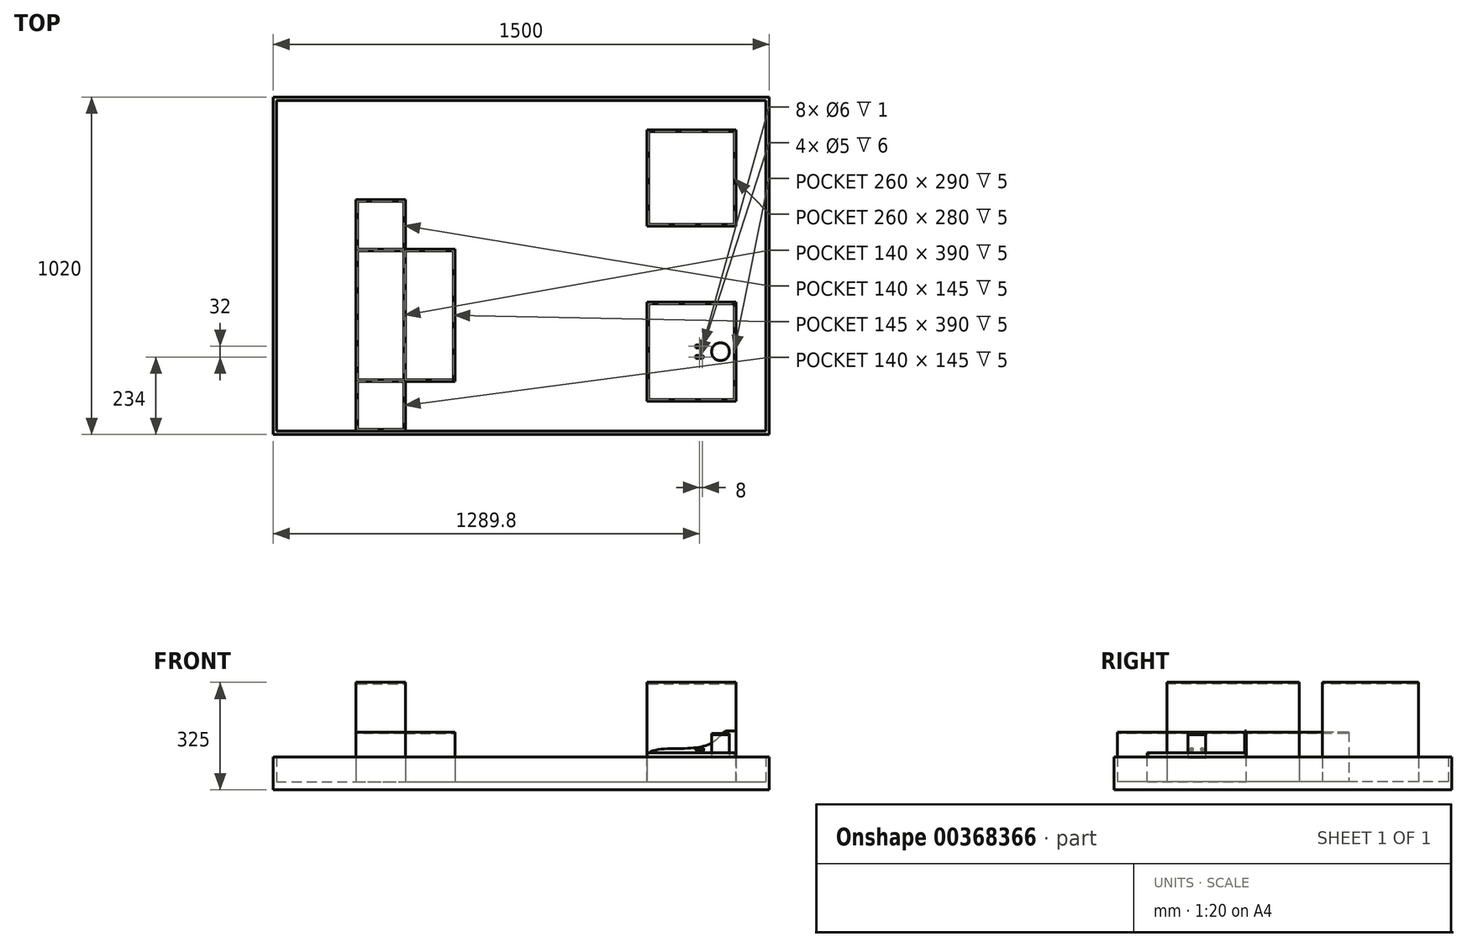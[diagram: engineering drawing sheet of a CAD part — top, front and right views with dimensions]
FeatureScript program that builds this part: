
annotation { "Feature Type Name" : "Feature", "Feature Type Description" : "" }
export const myFeature = defineFeature(function(context is Context, id is Id, definition is map)
    precondition{}
    {
        {
            var Q0;
            Q0=qCreatedBy(makeId("Top.planeOp"),FACE);
            var sketch = newSketch(context, id + "F0", { "sketchPlane" : qUnion([Q0])});
            skCircle(sketch, "E0", {"center": v(0, 0) * mm, "radius": 27.2 * mm});
            skSolve(sketch);
        }
        {
            var Q0;
            Q0=qSketchRegion(id+"F0",true);
            extrude(context, id + "F1", {"entities" : qUnion([Q0]), "depth" : 2.83 * mm});
        }
        {
            var Q0;
            Q0=makeQuery(id+"F1.opExtrude","CAP_FACE",FACE,{"disambiguationData":[OSD([sQuery(id+"F0.wireOp",EDGE,"E0")])],"isStart":false});
            var sketch = newSketch(context, id + "F2", { "sketchPlane" : qUnion([Q0])});
            skCircle(sketch, "E1", {"center": v(0, 0) * mm, "radius": 26.4 * mm});
            skSolve(sketch);
        }
        {
            var Q0;
            Q0=qSketchRegion(id+"F2",true);
            extrude(context, id + "F3", {"entities" : qUnion([Q0]), "operationType" : NewBodyOperationType.ADD, "depth" : 67.36 * mm});
        }
        {
            var Q0;
            Q0=makeQuery(id+"F3.opExtrude","CAP_FACE",FACE,{"disambiguationData":[OSD([sQuery(id+"F2.wireOp",EDGE,"E1")])],"isStart":false});
            var sketch = newSketch(context, id + "F4", { "sketchPlane" : qUnion([Q0])});
            skCircle(sketch, "E2", {"center": v(0, 0) * mm, "radius": 27.2 * mm});
            skSolve(sketch);
        }
        {
            var Q0;
            Q0=qSketchRegion(id+"F4",true);
            extrude(context, id + "F5", {"entities" : qUnion([Q0]), "operationType" : NewBodyOperationType.ADD, "depth" : 2.83 * mm});
        }
        {
            var Q0;
            Q0=makeQuery(id+"F5.opExtrude","CAP_FACE",FACE,{"disambiguationData":[OSD([sQuery(id+"F4.wireOp",EDGE,"E2")])],"isStart":false});
            var sketch = newSketch(context, id + "F6", { "sketchPlane" : qUnion([Q0])});
            skSolve(sketch);
        }
        {
            var Q0;
            Q0=qCreatedBy(makeId("Top.planeOp"),FACE);
            cPlane(context, id + "F7", {"entities" : qUnion([Q0]), "cplaneType" : CPlaneType.OFFSET, "offset" : 25 * mm, "width" : 150 * mm, "height" : 150 * mm});
        }
        {
            var Q0;
            Q0=qCreatedBy(makeId("Top.planeOp"),FACE);
            var sketch = newSketch(context, id + "F8", { "sketchPlane" : qUnion([Q0])});
            skLineSegment(sketch, "E3.bottom", {"start": v(-222.8, -150) * mm, "end": v(47.2, -150) * mm});
            skLineSegment(sketch, "E3.top", {"start": v(-222.8, 150) * mm, "end": v(47.2, 150) * mm});
            skLineSegment(sketch, "E3.left", {"start": v(-222.8, -150) * mm, "end": v(-222.8, 150) * mm});
            skLineSegment(sketch, "E3.right", {"start": v(47.2, -150) * mm, "end": v(47.2, 150) * mm});
            skSolve(sketch);
        }
        {
            var Q0;
            Q0=qSketchRegion(id+"F8",true);
            extrude(context, id + "F9", {"entities" : qUnion([Q0]), "oppositeDirection" : true, "depth" : 72 * mm});
        }
        {
            var Q0;
            Q0=makeQuery(id+"F9.opExtrude","CAP_FACE",FACE,{"disambiguationData":[OSD([sQuery(id+"F8.wireOp",EDGE,"E3.bottom"),sQuery(id+"F8.wireOp",EDGE,"E3.top"),sQuery(id+"F8.wireOp",EDGE,"E3.left"),sQuery(id+"F8.wireOp",EDGE,"E3.right")])],"isStart":true});
            var sketch = newSketch(context, id + "F10", { "sketchPlane" : qUnion([Q0])});
            skLineSegment(sketch, "E4.bottom", {"start": v(-222.8, -150) * mm, "end": v(47.2, -150) * mm});
            skLineSegment(sketch, "E4.top", {"start": v(-222.8, -145) * mm, "end": v(42.2, -145) * mm});
            skLineSegment(sketch, "E4.left", {"start": v(-222.8, -150) * mm, "end": v(-222.8, -145) * mm});
            skLineSegment(sketch, "E5.bottom", {"start": v(47.2, 150) * mm, "end": v(42.2, 150) * mm});
            skLineSegment(sketch, "E5.left", {"start": v(47.2, 150) * mm, "end": v(47.2, -150) * mm});
            skLineSegment(sketch, "E5.right", {"start": v(42.2, 150) * mm, "end": v(42.2, -145) * mm});
            skSolve(sketch);
        }
        {
            var Q0;
            Q0=qSketchRegion(id+"F10",true);
            extrude(context, id + "F11", {"entities" : qUnion([Q0]), "operationType" : NewBodyOperationType.ADD, "depth" : 15 * mm});
        }
        {
            var Q0;
            Q0=makeQuery(id+"F11.boolean.opBoolean","MERGE",FACE,{"derivedFrom":[makeQuery(id+"F9.opExtrude","SWEPT_FACE",FACE,{"disambiguationData":[OSD([sQuery(id+"F8.wireOp",EDGE,"E3.top")])]}),makeQuery(id+"F11.opExtrude","SWEPT_FACE",FACE,{"disambiguationData":[OSD([sQuery(id+"F10.wireOp",EDGE,"E5.bottom")])]})]});
            var sketch = newSketch(context, id + "F12", { "sketchPlane" : qUnion([Q0])});
            skLineSegment(sketch, "E6", {"start": v(-47.2, 81.36) * mm, "end": v(-21.31, 81.36) * mm});
            skFitSpline(sketch, "E7", {"points": [v(-21.31, 81.36) * mm, v(15.24, 52.01) * mm, v(114.14, 28.17) * mm, v(222.8, 0) * mm], "startDerivative": vector(181.02, 0.3) * mm, "endDerivative": vector(-1.73, -239.85) * mm});
            skLineSegment(sketch, "E8", {"start": v(-47.2, 81.36) * mm, "end": v(-47.2, -72) * mm});
            skLineSegment(sketch, "E9", {"start": v(-47.2, -72) * mm, "end": v(222.8, -72) * mm});
            skLineSegment(sketch, "E10", {"start": v(222.8, -72) * mm, "end": v(222.8, 0) * mm});
            skSolve(sketch);
        }
        {
            var Q0;
            Q0=qSketchRegion(id+"F12",true);
            extrude(context, id + "F13", {"entities" : qUnion([Q0]), "operationType" : NewBodyOperationType.ADD, "oppositeDirection" : true, "depth" : 5 * mm});
        }
        {
            var Q0;
            Q0=makeQuery(id+"F9.opExtrude","CAP_FACE",FACE,{"disambiguationData":[OSD([sQuery(id+"F8.wireOp",EDGE,"E3.bottom"),sQuery(id+"F8.wireOp",EDGE,"E3.top"),sQuery(id+"F8.wireOp",EDGE,"E3.left"),sQuery(id+"F8.wireOp",EDGE,"E3.right")])],"isStart":true});
            var sketch = newSketch(context, id + "F14", { "sketchPlane" : qUnion([Q0])});
            skLineSegment(sketch, "E11.bottom", {"start": v(-222.8, 145) * mm, "end": v(-217.8, 145) * mm});
            skLineSegment(sketch, "E11.top", {"start": v(-222.8, -145) * mm, "end": v(-217.8, -145) * mm});
            skLineSegment(sketch, "E11.left", {"start": v(-222.8, 145) * mm, "end": v(-222.8, -145) * mm});
            skLineSegment(sketch, "E11.right", {"start": v(-217.8, 145) * mm, "end": v(-217.8, -145) * mm});
            skSolve(sketch);
        }
        {
            var Q0;
            Q0=qSketchRegion(id+"F14",true);
            extrude(context, id + "F15", {"entities" : qUnion([Q0]), "operationType" : NewBodyOperationType.ADD, "depth" : 5 * mm});
        }
        {
            var Q0;
            Q0=makeQuery(id+"F9.opExtrude","CAP_FACE",FACE,{"disambiguationData":[OSD([sQuery(id+"F8.wireOp",EDGE,"E3.bottom"),sQuery(id+"F8.wireOp",EDGE,"E3.top"),sQuery(id+"F8.wireOp",EDGE,"E3.left"),sQuery(id+"F8.wireOp",EDGE,"E3.right")])],"isStart":false});
            var sketch = newSketch(context, id + "F16", { "sketchPlane" : qUnion([Q0])});
            skLineSegment(sketch, "E12.bottom", {"start": v(147.2, 250) * mm, "end": v(-1352.8, 250) * mm});
            skLineSegment(sketch, "E12.top", {"start": v(147.2, -770) * mm, "end": v(-1352.8, -770) * mm});
            skLineSegment(sketch, "E12.left", {"start": v(147.2, 250) * mm, "end": v(147.2, -770) * mm});
            skLineSegment(sketch, "E12.right", {"start": v(-1352.8, 250) * mm, "end": v(-1352.8, -770) * mm});
            skSolve(sketch);
        }
        {
            var Q0;
            Q0=qSketchRegion(id+"F16",true);
            extrude(context, id + "F17", {"entities" : qUnion([Q0]), "operationType" : NewBodyOperationType.ADD, "depth" : 25 * mm});
        }
        {
            var Q0;
            Q0=makeQuery(id+"F17.opExtrude","CAP_FACE",FACE,{"disambiguationData":[OSD([sQuery(id+"F16.wireOp",EDGE,"E12.bottom"),sQuery(id+"F16.wireOp",EDGE,"E12.top"),sQuery(id+"F16.wireOp",EDGE,"E12.left"),sQuery(id+"F16.wireOp",EDGE,"E12.right")])],"isStart":true});
            var sketch = newSketch(context, id + "F18", { "sketchPlane" : qUnion([Q0])});
            skLineSegment(sketch, "E13.bottom", {"start": v(-222.8, 670) * mm, "end": v(47.2, 670) * mm});
            skLineSegment(sketch, "E13.top", {"start": v(-222.8, 380) * mm, "end": v(47.2, 380) * mm});
            skLineSegment(sketch, "E13.left", {"start": v(-222.8, 670) * mm, "end": v(-222.8, 380) * mm});
            skLineSegment(sketch, "E13.right", {"start": v(47.2, 670) * mm, "end": v(47.2, 380) * mm});
            skSolve(sketch);
        }
        {
            var Q0;
            Q0=qSketchRegion(id+"F18",true);
            extrude(context, id + "F19", {"entities" : qUnion([Q0]), "operationType" : NewBodyOperationType.ADD, "depth" : 300 * mm});
        }
        {
            var Q0;
            Q0=makeQuery(id+"F19.opExtrude","CAP_FACE",FACE,{"disambiguationData":[OSD([sQuery(id+"F18.wireOp",EDGE,"E13.bottom"),sQuery(id+"F18.wireOp",EDGE,"E13.top"),sQuery(id+"F18.wireOp",EDGE,"E13.left"),sQuery(id+"F18.wireOp",EDGE,"E13.right")])],"isStart":false});
            var sketch = newSketch(context, id + "F20", { "sketchPlane" : qUnion([Q0])});
            skLineSegment(sketch, "E14.bottom", {"start": v(-217.8, 665) * mm, "end": v(42.2, 665) * mm});
            skLineSegment(sketch, "E14.top", {"start": v(-217.8, 385) * mm, "end": v(42.2, 385) * mm});
            skLineSegment(sketch, "E14.left", {"start": v(-217.8, 665) * mm, "end": v(-217.8, 385) * mm});
            skLineSegment(sketch, "E14.right", {"start": v(42.2, 665) * mm, "end": v(42.2, 385) * mm});
            skSolve(sketch);
        }
        {
            var Q0;
            Q0=qSketchRegion(id+"F20",true);
            extrude(context, id + "F21", {"entities" : qUnion([Q0]), "operationType" : NewBodyOperationType.REMOVE, "oppositeDirection" : true, "depth" : 5 * mm});
        }
        {
            var Q0;
            Q0=makeQuery(id+"F17.opExtrude","CAP_FACE",FACE,{"disambiguationData":[OSD([sQuery(id+"F16.wireOp",EDGE,"E12.bottom"),sQuery(id+"F16.wireOp",EDGE,"E12.top"),sQuery(id+"F16.wireOp",EDGE,"E12.left"),sQuery(id+"F16.wireOp",EDGE,"E12.right")])],"isStart":true});
            var sketch = newSketch(context, id + "F22", { "sketchPlane" : qUnion([Q0])});
            skLineSegment(sketch, "E15.bottom", {"start": v(-1352.8, 770) * mm, "end": v(147.2, 770) * mm});
            skLineSegment(sketch, "E15.top", {"start": v(-1352.8, -250) * mm, "end": v(147.2, -250) * mm});
            skLineSegment(sketch, "E15.left", {"start": v(-1352.8, 770) * mm, "end": v(-1352.8, -250) * mm});
            skLineSegment(sketch, "E15.right", {"start": v(147.2, 770) * mm, "end": v(147.2, -250) * mm});
            skLineSegment(sketch, "E16.bottom", {"start": v(-1342.8, 760) * mm, "end": v(137.2, 760) * mm});
            skLineSegment(sketch, "E16.top", {"start": v(-1342.8, -240) * mm, "end": v(137.2, -240) * mm});
            skLineSegment(sketch, "E16.left", {"start": v(-1342.8, 760) * mm, "end": v(-1342.8, -240) * mm});
            skLineSegment(sketch, "E16.right", {"start": v(137.2, 760) * mm, "end": v(137.2, -240) * mm});
            skSolve(sketch);
        }
        {
            var Q0;
            Q0=qSketchRegion(id+"F22",true);
            extrude(context, id + "F23", {"entities" : qUnion([Q0]), "operationType" : NewBodyOperationType.ADD, "depth" : 75 * mm});
        }
        {
            var Q0;
            Q0=makeQuery(id+"F17.opExtrude","CAP_FACE",FACE,{"disambiguationData":[OSD([sQuery(id+"F16.wireOp",EDGE,"E12.bottom"),sQuery(id+"F16.wireOp",EDGE,"E12.top"),sQuery(id+"F16.wireOp",EDGE,"E12.left"),sQuery(id+"F16.wireOp",EDGE,"E12.right")])],"isStart":true});
            var sketch = newSketch(context, id + "F24", { "sketchPlane" : qUnion([Q0])});
            skLineSegment(sketch, "E17.bottom", {"start": v(-1102.8, 460) * mm, "end": v(-952.8, 460) * mm});
            skLineSegment(sketch, "E17.top", {"start": v(-1102.8, -240) * mm, "end": v(-952.8, -240) * mm});
            skLineSegment(sketch, "E17.left", {"start": v(-1102.8, 460) * mm, "end": v(-1102.8, -240) * mm});
            skLineSegment(sketch, "E17.right", {"start": v(-952.8, 460) * mm, "end": v(-952.8, 310) * mm});
            skLineSegment(sketch, "E18.bottom", {"start": v(-952.8, 310) * mm, "end": v(-802.8, 310) * mm});
            skLineSegment(sketch, "E18.top", {"start": v(-952.8, -90) * mm, "end": v(-802.8, -90) * mm});
            skLineSegment(sketch, "E18.right", {"start": v(-802.8, 310) * mm, "end": v(-802.8, -90) * mm});
            skLineSegment(sketch, "E19.trimOffspring", {"start": v(-952.8, -90) * mm, "end": v(-952.8, -240) * mm});
            skSolve(sketch);
        }
        {
            var Q0;
            Q0=qSketchRegion(id+"F24",true);
            extrude(context, id + "F25", {"entities" : qUnion([Q0]), "operationType" : NewBodyOperationType.ADD, "depth" : 150 * mm});
        }
        {
            var Q0;
            Q0=makeQuery(id+"F25.opExtrude","CAP_FACE",FACE,{"disambiguationData":[OSD([sQuery(id+"F24.wireOp",EDGE,"E17.bottom"),sQuery(id+"F24.wireOp",EDGE,"E17.top"),sQuery(id+"F24.wireOp",EDGE,"E17.left"),sQuery(id+"F24.wireOp",EDGE,"E17.right"),sQuery(id+"F24.wireOp",EDGE,"E18.bottom"),sQuery(id+"F24.wireOp",EDGE,"E18.top"),sQuery(id+"F24.wireOp",EDGE,"E18.right"),sQuery(id+"F24.wireOp",EDGE,"E19.trimOffspring")])],"isStart":false});
            var sketch = newSketch(context, id + "F26", { "sketchPlane" : qUnion([Q0])});
            skLineSegment(sketch, "E20.bottom", {"start": v(-952.8, 310) * mm, "end": v(-1102.8, 310) * mm});
            skLineSegment(sketch, "E20.top", {"start": v(-952.8, -90) * mm, "end": v(-1102.8, -90) * mm});
            skLineSegment(sketch, "E20.left", {"start": v(-952.8, 310) * mm, "end": v(-952.8, -90) * mm});
            skLineSegment(sketch, "E20.right", {"start": v(-1102.8, 310) * mm, "end": v(-1102.8, -90) * mm});
            skSolve(sketch);
        }
        {
            var Q0;
            Q0=qSketchRegion(id+"F26",true);
            extrude(context, id + "F27", {"entities" : qUnion([Q0]), "operationType" : NewBodyOperationType.ADD, "depth" : 150 * mm});
        }
        {
            var Q0;
            Q0=makeQuery(id+"F27.opExtrude","CAP_FACE",FACE,{"disambiguationData":[OSD([sQuery(id+"F26.wireOp",EDGE,"E20.bottom"),sQuery(id+"F26.wireOp",EDGE,"E20.top"),sQuery(id+"F26.wireOp",EDGE,"E20.left"),sQuery(id+"F26.wireOp",EDGE,"E20.right")])],"isStart":false});
            var sketch = newSketch(context, id + "F28", { "sketchPlane" : qUnion([Q0])});
            skLineSegment(sketch, "E21.bottom", {"start": v(-1097.8, 305) * mm, "end": v(-957.8, 305) * mm});
            skLineSegment(sketch, "E21.top", {"start": v(-1097.8, -85) * mm, "end": v(-957.8, -85) * mm});
            skLineSegment(sketch, "E21.left", {"start": v(-1097.8, 305) * mm, "end": v(-1097.8, -85) * mm});
            skLineSegment(sketch, "E21.right", {"start": v(-957.8, 305) * mm, "end": v(-957.8, -85) * mm});
            skSolve(sketch);
        }
        {
            var Q0;
            Q0=qSketchRegion(id+"F28",true);
            extrude(context, id + "F29", {"entities" : qUnion([Q0]), "operationType" : NewBodyOperationType.REMOVE, "oppositeDirection" : true, "depth" : 5 * mm});
        }
        {
            var Q0;
            {var subQ0=sQuery(id+"F24.wireOp",EDGE,"E17.left");var subQ1=sQuery(id+"F24.wireOp",EDGE,"E18.bottom");var subQ2=sQuery(id+"F24.wireOp",EDGE,"E17.right");var subQ3=sQuery(id+"F24.wireOp",EDGE,"E17.bottom");var subQ4=makeQuery(id+"F25.opExtrude","CAP_FACE",FACE,{"disambiguationData":[OSD([subQ3,sQuery(id+"F24.wireOp",EDGE,"E17.top"),subQ0,subQ2,subQ1,sQuery(id+"F24.wireOp",EDGE,"E18.top"),sQuery(id+"F24.wireOp",EDGE,"E18.right"),sQuery(id+"F24.wireOp",EDGE,"E19.trimOffspring")])],"isStart":false});Q0=makeQuery(id+"F27.boolean.opBoolean","SPLIT",FACE,{"disambiguationData":[TD([makeQuery(id+"F25.opExtrude","SWEPT_FACE",FACE,{"disambiguationData":[OSD([subQ3])]})])],"derivedFrom":subQ4});}
            var sketch = newSketch(context, id + "F30", { "sketchPlane" : qUnion([Q0])});
            skLineSegment(sketch, "E22.bottom", {"start": v(-1097.8, 455) * mm, "end": v(-957.8, 455) * mm});
            skLineSegment(sketch, "E22.top", {"start": v(-1097.8, 310) * mm, "end": v(-957.8, 310) * mm});
            skLineSegment(sketch, "E22.left", {"start": v(-1097.8, 455) * mm, "end": v(-1097.8, 310) * mm});
            skLineSegment(sketch, "E22.right", {"start": v(-957.8, 455) * mm, "end": v(-957.8, 310) * mm});
            skLineSegment(sketch, "E23.bottom", {"start": v(-952.8, 305) * mm, "end": v(-807.8, 305) * mm});
            skLineSegment(sketch, "E23.top", {"start": v(-952.8, -85) * mm, "end": v(-807.8, -85) * mm});
            skLineSegment(sketch, "E23.left", {"start": v(-952.8, 305) * mm, "end": v(-952.8, -85) * mm});
            skLineSegment(sketch, "E23.right", {"start": v(-807.8, 305) * mm, "end": v(-807.8, -85) * mm});
            skLineSegment(sketch, "E24.bottom", {"start": v(-1097.8, -90) * mm, "end": v(-957.8, -90) * mm});
            skLineSegment(sketch, "E24.top", {"start": v(-1097.8, -235) * mm, "end": v(-957.8, -235) * mm});
            skLineSegment(sketch, "E24.left", {"start": v(-1097.8, -90) * mm, "end": v(-1097.8, -235) * mm});
            skLineSegment(sketch, "E24.right", {"start": v(-957.8, -90) * mm, "end": v(-957.8, -235) * mm});
            skSolve(sketch);
        }
        {
            var Q0;
            Q0=qSketchRegion(id+"F30",true);
            extrude(context, id + "F31", {"entities" : qUnion([Q0]), "operationType" : NewBodyOperationType.REMOVE, "oppositeDirection" : true, "depth" : 5 * mm});
        }
        {
            var Q0;
            Q0=qCreatedBy(id+"F7.planeOp",FACE);
            var sketch = newSketch(context, id + "F32", { "sketchPlane" : qUnion([Q0])});
            skLineSegment(sketch, "E25", {"start": v(0, 0) * mm, "end": v(-90, 0) * mm, "construction": true});
            skLineSegment(sketch, "E26.bottom", {"start": v(-74.5, -12) * mm, "end": v(-55, -12) * mm});
            skLineSegment(sketch, "E26.top", {"start": v(-74.5, -20) * mm, "end": v(-55, -20) * mm});
            skLineSegment(sketch, "E26.left", {"start": v(-74.5, -12) * mm, "end": v(-74.5, -13) * mm});
            skPoint(sketch, "E27.visualSharp", {"position": v(-51, -12) * mm});
            skPoint(sketch, "E28.visualSharp", {"position": v(-51, -20) * mm});
            skCircle(sketch, "E29", {"center": v(-55, -16) * mm, "radius": 3 * mm});
            skLineSegment(sketch, "E30", {"start": v(-59, -3.98) * mm, "end": v(-59, -18.08) * mm, "construction": true});
            skCircle(sketch, "E31.MirrorC", {"center": v(-63, -16) * mm, "radius": 3 * mm});
            skLineSegment(sketch, "E32.bottom", {"start": v(-74.5, -13) * mm, "end": v(-65.65, -13) * mm});
            skLineSegment(sketch, "E32.top", {"start": v(-74.5, -19) * mm, "end": v(-65.65, -19) * mm});
            skArc(sketch, "E33", {"start": v(-65.65, -13) * mm, "mid": v(-67, -16) * mm, "end": v(-65.65, -19) * mm});
            skLineSegment(sketch, "E34.trimOffspring", {"start": v(-74.5, -19) * mm, "end": v(-74.5, -20) * mm});
            skArc(sketch, "E35.trimOffspring", {"start": v(-55, -20) * mm, "mid": v(-51, -16) * mm, "end": v(-55, -12) * mm});
            skLineSegment(sketch, "E36.MirrorCS", {"start": v(-74.5, 12) * mm, "end": v(-74.5, 13) * mm});
            skLineSegment(sketch, "E37.MirrorCS", {"start": v(-74.5, 19) * mm, "end": v(-74.5, 20) * mm});
            skPoint(sketch, "E38.MirrorP", {"position": v(-51, 12) * mm});
            skLineSegment(sketch, "E39.MirrorCS", {"start": v(-74.5, 12) * mm, "end": v(-55, 12) * mm});
            skPoint(sketch, "E40.MirrorP", {"position": v(-51, 20) * mm});
            skArc(sketch, "E41.MirrorCS", {"start": v(-65.65, 13) * mm, "mid": v(-67, 16) * mm, "end": v(-65.65, 19) * mm});
            skArc(sketch, "E42.MirrorCS", {"start": v(-55, 20) * mm, "mid": v(-51, 16) * mm, "end": v(-55, 12) * mm});
            skLineSegment(sketch, "E43.MirrorCS", {"start": v(-74.5, 20) * mm, "end": v(-55, 20) * mm});
            skCircle(sketch, "E44.MirrorC", {"center": v(-55, 16) * mm, "radius": 3 * mm});
            skCircle(sketch, "E45.MirrorC", {"center": v(-63, 16) * mm, "radius": 3 * mm});
            skLineSegment(sketch, "E46.MirrorCS", {"start": v(-74.5, 19) * mm, "end": v(-65.65, 19) * mm});
            skLineSegment(sketch, "E47.MirrorCS", {"start": v(-74.5, 13) * mm, "end": v(-65.65, 13) * mm});
            skSolve(sketch);
        }
        {
            var Q0;
            Q0=qSketchRegion(id+"F32",true);
            var Q1;
            Q1=qSketchRegion(id+"F35",true);
            extrude(context, id + "F33", {"entities" : qUnion([Q0, Q1]), "endBound" : BoundingType.SYMMETRIC, "depth" : 8 * mm});
        }
        {
            var Q0;
            Q0=makeQuery(id+"F33.opExtrude","CAP_EDGE",EDGE,{"disambiguationData":[OSD([sQuery(id+"F32.wireOp",EDGE,"E34.trimOffspring")])],"isStart":false});
            var Q1;
            Q1=makeQuery(id+"F33.opExtrude","CAP_EDGE",EDGE,{"disambiguationData":[OSD([sQuery(id+"F32.wireOp",EDGE,"E26.left")])],"isStart":false});
            var Q2;
            Q2=makeQuery(id+"F33.opExtrude","CAP_EDGE",EDGE,{"disambiguationData":[OSD([sQuery(id+"F32.wireOp",EDGE,"E34.trimOffspring")])],"isStart":true});
            var Q3;
            Q3=makeQuery(id+"F33.opExtrude","CAP_EDGE",EDGE,{"disambiguationData":[OSD([sQuery(id+"F32.wireOp",EDGE,"E26.left")])],"isStart":true});
            var Q4;
            Q4=makeQuery(id+"F33.opExtrude","CAP_EDGE",EDGE,{"disambiguationData":[OSD([sQuery(id+"F32.wireOp",EDGE,"E36.MirrorCS")])],"isStart":false});
            var Q5;
            Q5=makeQuery(id+"F33.opExtrude","CAP_EDGE",EDGE,{"disambiguationData":[OSD([sQuery(id+"F32.wireOp",EDGE,"E37.MirrorCS")])],"isStart":false});
            var Q6;
            Q6=makeQuery(id+"F33.opExtrude","CAP_EDGE",EDGE,{"disambiguationData":[OSD([sQuery(id+"F32.wireOp",EDGE,"E37.MirrorCS")])],"isStart":true});
            var Q7;
            Q7=makeQuery(id+"F33.opExtrude","CAP_EDGE",EDGE,{"disambiguationData":[OSD([sQuery(id+"F32.wireOp",EDGE,"E36.MirrorCS")])],"isStart":true});
            fillet(context, id + "F34", {"entities" : qUnion([Q0, Q1, Q2, Q3, Q4, Q5, Q6, Q7]), "radius" : 4 * mm, "tangentPropagation" : true, "allowEdgeOverflow" : false});
        }
        {
            var Q0;
            Q0=makeQuery(id+"F33.opExtrude","SWEPT_FACE",FACE,{"disambiguationData":[OSD([sQuery(id+"F32.wireOp",EDGE,"E26.top")])]});
            var sketch = newSketch(context, id + "F35", { "sketchPlane" : qUnion([Q0])});
            skCircle(sketch, "E48", {"center": v(-70.5, 25) * mm, "radius": 3 * mm});
            skSolve(sketch);
        }
        {
            var Q0;
            Q0=qSketchRegion(id+"F35",true);
            var Q1;
            Q1=makeQuery(id+"F33.opExtrude","SWEPT_FACE",FACE,{"disambiguationData":[OSD([sQuery(id+"F32.wireOp",EDGE,"E26.bottom")])]});
            extrude(context, id + "F36", {"entities" : qUnion([Q0]), "operationType" : NewBodyOperationType.ADD, "endBound" : BoundingType.UP_TO_SURFACE, "oppositeDirection" : true, "endBoundEntityFace" : qUnion([Q1]), "depth" : 25 * mm});
        }
        {
            var Q0;
            Q0=makeQuery(id+"F33.opExtrude","SWEPT_FACE",FACE,{"disambiguationData":[OSD([sQuery(id+"F32.wireOp",EDGE,"E43.MirrorCS")])]});
            var sketch = newSketch(context, id + "F37", { "sketchPlane" : qUnion([Q0])});
            skCircle(sketch, "E49", {"center": v(70.5, 25) * mm, "radius": 3 * mm});
            skSolve(sketch);
        }
        {
            var Q0;
            Q0=qSketchRegion(id+"F37",true);
            var Q1;
            Q1=makeQuery(id+"F33.opExtrude","SWEPT_FACE",FACE,{"disambiguationData":[OSD([sQuery(id+"F32.wireOp",EDGE,"E39.MirrorCS")])]});
            extrude(context, id + "F38", {"entities" : qUnion([Q0]), "operationType" : NewBodyOperationType.ADD, "endBound" : BoundingType.UP_TO_SURFACE, "oppositeDirection" : true, "endBoundEntityFace" : qUnion([Q1]), "depth" : 25 * mm});
        }
        {
            var Q0;
            Q0=qCreatedBy(id+"F7.planeOp",FACE);
            var sketch = newSketch(context, id + "F39", { "sketchPlane" : qUnion([Q0])});
            skCircle(sketch, "E50", {"center": v(-55, 16) * mm, "radius": 3 * mm});
            skCircle(sketch, "E51", {"center": v(-63, 16) * mm, "radius": 2.5 * mm});
            skCircle(sketch, "E52", {"center": v(-63, 16) * mm, "radius": 3 * mm});
            skCircle(sketch, "E53", {"center": v(-55, 16) * mm, "radius": 2.5 * mm});
            skSolve(sketch);
        }
        {
            var Q0;
            Q0=qSketchRegion(id+"F39",true);
            extrude(context, id + "F40", {"entities" : qUnion([Q0]), "operationType" : NewBodyOperationType.ADD, "endBound" : BoundingType.SYMMETRIC, "depth" : 6 * mm});
        }
        {
            var Q0;
            Q0=qCreatedBy(id+"F7.planeOp",FACE);
            var sketch = newSketch(context, id + "F41", { "sketchPlane" : qUnion([Q0])});
            skCircle(sketch, "E54", {"center": v(-63, -16) * mm, "radius": 2.5 * mm});
            skCircle(sketch, "E55", {"center": v(-63, -16) * mm, "radius": 3 * mm});
            skCircle(sketch, "E56", {"center": v(-55, -16) * mm, "radius": 2.5 * mm});
            skCircle(sketch, "E57", {"center": v(-55, -16) * mm, "radius": 3 * mm});
            skSolve(sketch);
        }
        {
            var Q0;
            Q0=qSketchRegion(id+"F41",true);
            extrude(context, id + "F42", {"entities" : qUnion([Q0]), "operationType" : NewBodyOperationType.ADD, "endBound" : BoundingType.SYMMETRIC, "depth" : 6 * mm});
        }
    });
